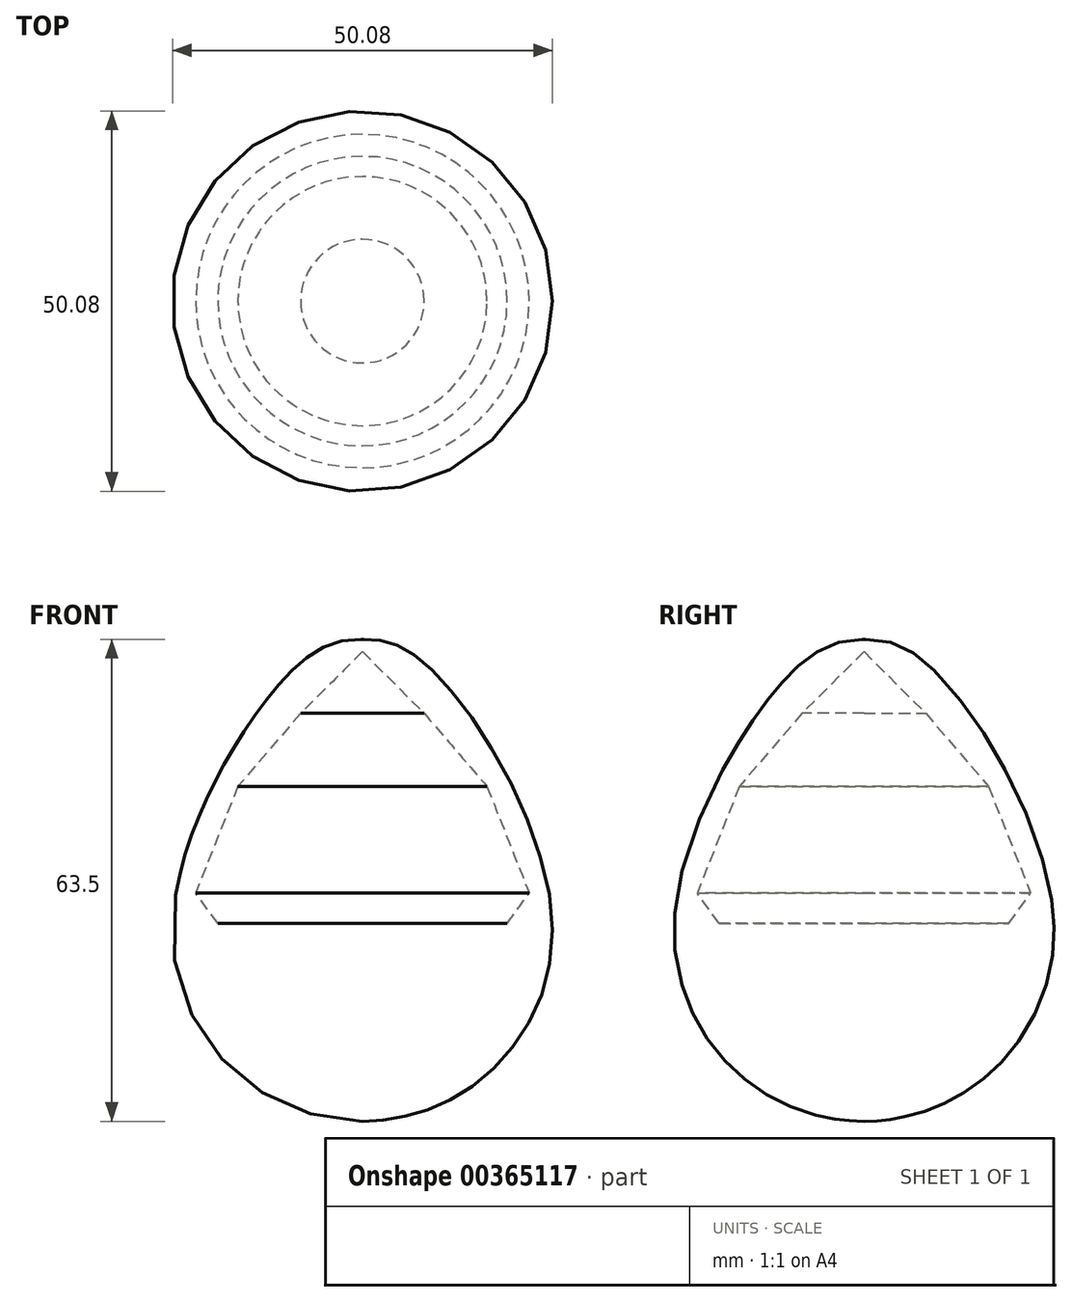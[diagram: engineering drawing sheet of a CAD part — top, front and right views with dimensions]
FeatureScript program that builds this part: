
annotation { "Feature Type Name" : "Feature", "Feature Type Description" : "" }
export const myFeature = defineFeature(function(context is Context, id is Id, definition is map)
    precondition{}
    {
        {
            var Q0;
            Q0=qCreatedBy(makeId("Front.planeOp"),FACE);
            var sketch = newSketch(context, id + "F0", { "sketchPlane" : qUnion([Q0])});
            skFitSpline(sketch, "E0", {"points": [v(-19.35, -9.7) * mm, v(-5.04, -5.21) * mm, v(5.67, 16.34) * mm, v(-9.99, 49.58) * mm, v(-19.35, 53.8) * mm], "startDerivative": vector(59.94, 0) * mm, "endDerivative": vector(-55.95, -0.58) * mm});
            skLineSegment(sketch, "E1", {"start": v(-19.35, -9.7) * mm, "end": v(-19.35, 16.34) * mm});
            skLineSegment(sketch, "E2", {"start": v(-19.35, 16.34) * mm, "end": v(-0.29, 16.34) * mm});
            skLineSegment(sketch, "E3", {"start": v(-11.21, 44.02) * mm, "end": v(-19.35, 52.16) * mm});
            skLineSegment(sketch, "E4", {"start": v(-19.35, 52.16) * mm, "end": v(-19.35, 53.8) * mm});
            skLineSegment(sketch, "E5", {"start": v(-11.21, 44.02) * mm, "end": v(-2.94, 34.4) * mm});
            skLineSegment(sketch, "E6", {"start": v(-2.94, 34.4) * mm, "end": v(2.61, 20.37) * mm});
            skLineSegment(sketch, "E7", {"start": v(2.61, 20.37) * mm, "end": v(-0.29, 16.34) * mm});
            skLineSegment(sketch, "E8", {"start": v(-19.35, 53.8) * mm, "end": v(-19.35, -9.7) * mm, "construction": true});
            skSolve(sketch);
        }
        {
            var Q0;
            Q0=makeQuery(id+"F0.imprint","IMPRINT",FACE,{"disambiguationData":[TD([[makeQuery(id+"F0.imprint","IMPRINT",EDGE,{"derivedFrom":sQuery(id+"F0.wireOp",EDGE,"E0")}),1.0]])]});
            var Q1;
            Q1=sQuery(id+"F0.wireOp",EDGE,"E8");
            revolve(context, id + "F1", {"entities" : qUnion([Q0]), "axis" : qUnion([Q1]), "revolveType" : RevolveType.FULL});
        }
    });
